# Revit family: 2059297 Lighting Fixture_Sylvania_Ascent 100 Arch(160)-Very High Output_Ceiling Recessed
name_source: partatom
category: Lighting Fixtures
revit_build: Autodesk Revit 2017 (Build: 20190507_1515(x64)
units: mm (PartAtom-declared; Revit-internal decimal feet)

## family parameters
Cut with Voids When Loaded = No
Host = Face
Light Source = Yes
OmniClass Number = 23.80.70.11.17
OmniClass Title = Specialized Lighting by Location or Use
Part Type = Normal
Room Calculation Point = No
Round Connector Dimension = Use Diameter
Shared = No

## types (1)
- Asct100 Arch VVHO 3K STD 160
    Accessory Material = Aluminum_Sylvania_Ascent_White
    Aperture = 160 mm
    Apparent Load = 35 VA
    Assembly Code = D5020200
    Body Material = Aluminum_Sylvania_Ascent_White
    Catalog Number = 2059297 Asct100 Arch VVHO 3K STD 160
    Color Filter = 16777215
    Cutout Diameter = 176 mm
    Default Elevation = 0 mm  [stored 0 ft]
    Description = Direct LED retro fit for original LED 100 Arch (160) single CFL lamp offering Matching lumen levels and improved light distribution of original LED 100 CFL lamp equivalents Typically half the power consumption compared to CFL Up to 112lm/W 160mm aperture Architectural reflector accepts range of glass accessories from existing LED 100 Arch 160 offering HE, HO and VHO versions equivalent of single 1 x 18W, 1 x 32W, 1 x 42W
 Additional VVHO versions which offer the performance circa 2 x 32W equivalent
    Diameter = 189 mm  [stored 0.620079 ft]
    Diffuser Material = Polycarbonate_Sylvania_Ascent_Clear
    Diffuser Radius = 73 mm
    Dimming Lamp Color Temperature Shift = <None>
    Drive Current = 1400mA
    Emit Shape Visible in Rendering = No
    Emit from Circle Diameter = 146 mm
    Glow Wire Test = 850 °C
    Height = 94 mm  [stored 0.308399 ft]
    IK Rating = IK02
    IP Rating = IP44
    Lamp = Integrated LED
    Life = 50 000h
    Manufacturer = Feilo-Sylvania Group
    Model = Asct100 Arch VVHO 3K STD 160
    Photometric Web File = 2059297_Asct100ArchVVHO3KSTD160-189730.ies
    Product Family = Ascent 100 Arch (160) - Very High Output
    Product Page URL = https://www.sylvania-lighting.com
    Radius = 94.5 mm  [stored 0.310039 ft]
    Reflector Material = Aluminium_Sylvania_Ascent_Silver
    Reflector Radius = 80 mm
    Tilt Angle = -90°
    URL = https://www.sylvania-lighting.com
    Voltage = 240 V
    Voltage Comments = UNV (Universal Voltage; 220-240 Volt)

note: [stored X ft] marks values corroborated as IEEE doubles in the binary element streams (Revit-internal decimal feet)

## geometry (parser evidence)
native form markers: Sweep x3
no freeform markers — native parametric forms only
